# Revit family: Toilet-Elongated-Right_Height-American_Standard-Townsend-2922A.10X_Series
name_source: partatom
category: Plumbing Fixtures
units: mm (PartAtom-declared; Revit-internal decimal feet)

## family parameters
Always vertical = No
Cut with Voids When Loaded = No
OmniClass Number = 23.45.05.21.11.11
OmniClass Title = Water Operated Water Closets
Part Type = Normal
Room Calculation Point = No
Round Connector Dimension = Use Radius
Shared = Yes
Work Plane-Based = Yes

## types (3) — shared parameters
ADA Compliant = Yes
ASME A112.19.2/CSA B45.1 = Yes
Assembly Code = D2010110
Bowl Shape = Elongated
CEC Compliant = Yes
CW Connection = Yes
CWFU = 10
CalGreen Compliant = Yes
Cold Water Connection Diameter = 1/2"
Cold Water Connection Height = 8"
Cold Water Connection Radius = 1/4"
Cold Water Connection Width = 6"
Default Elevation = 0"
Finish - Lever = Metal-American Standard-002-Polished Chrome
Finished Wall to C/L of Outlet = 12"
Finished Wall to Outlet Constraint = 12"
Flush Rate = 1.28Gpf (4.8Lpf)
HW Connection = No
Height = 29 3/4"
Installation Type = Floor Mounted
Length = 30 3/16"
Manufacturer = American Standard
Price = Prices may vary. Please consult Manufacturer Representative for most up-to-date price list.
Product Documentation Link = https://americanstandard.box.com
Product Page URL = https://www.americanstandard-us.com
Revised Date = 03/07/2022
URL = http://www.americanstandard-us.com
US EPA WaterSense® Specification for HETs = Yes
Vent Connection = No
WFU = 10
Warranty Information = 10 Year Limited
Waste Connection = Yes
Width = 16 7/8"
zero-valued in all types: HWFU

## per-type parameters (varying)
| type | Description | Finish | Left Lever | Material | Right Lever | Waste Connection Diameter | Waste Connection Radius |
| 2922A104.020 | Townsend Vormax Right Height Elongated One-Piece Toilet With Seat | Vitreous China-American Standard-020-White | Yes | Vitreous China-American Standard-020-White | No | 2" | 1" |
| 2922A105.020 | Townsend Vormax Right Height Elongated One-Piece Toilet With Seat and Right Hand Trip Lever | Vitreous China-American Standard-020-White | No | Vitreous China-American Standard-020-White | Yes | 2 1/16" | 1 1/32" |
| 2922A104.222 | Townsend Vormax Right Height Elongated One-Piece Toilet With Seat | Vitreous China-American Standard-222-Linen | Yes | Vitreous China-American Standard-222-Linen | No | 2 1/16" | 1 1/32" |

note: column(s) folded — value = type name in every type: Model

## geometry (parser evidence)
native form markers: Sweep x2
no freeform markers — native parametric forms only
